# Revit family: FP-Revit19-en-OS60NMLG1-CombinationSteamOven-0-90003174A-AU-NZ-CN-IE-UK
name_source: partatom
category: Specialty Equipment
units: mm (PartAtom-declared; Revit-internal decimal feet)

## family parameters
Always vertical = Yes
Cut with Voids When Loaded = Yes
OmniClass Number = 23.40.40.14.17.11
OmniClass Title = Cookers, Ovens, Stoves
Part Type = Normal
Room Calculation Point = No
Round Connector Dimension = Use Diameter
Shared = No
Work Plane-Based = No

## types (1)
- OS60NMLG1
    Cavity - Depth = 550 mm
    Cavity - Height = 440 mm  [stored 1.44357 ft]
    Cavity - Width = 560 mm
    Chassis - Depth = 545 mm  [stored 1.78806 ft]
    Chassis - Height = 435 mm  [stored 1.42717 ft]
    Chassis - Width = 556 mm  [stored 1.82415 ft]
    Connector Description - Electrical = 220-240V, 50Hz ,15A
    Description = Combination Steam Oven, 60cm, 18 Function
    Manufacturer = Fisher & Paykel Appliances
    Material - Body = Fisher & Paykel - Grey
    Material - Dial = Fisher & Paykel - Aluminium, Dark, Matt
    Material - Glass = Fisher & Paykel - Glass, Grey
    Material - Handle = Fisher & Paykel - Aluminium, Dark
    Material - Structure = Fisher & Paykel - Black
    Material - Trim = Fisher & Paykel - Aluminium, Dark
    Model = OS60NMLG1
    Opening - Height = 460 mm  [stored 1.50919 ft]
    Product - Depth (Exc. Handles) = 565 mm  [stored 1.85367 ft]
    Product - Height = 458 mm
    Product - Width = 596 mm
    URL = www.fisherpaykel.com
    Visibility - Clearance Required = Yes

note: [stored X ft] marks values corroborated as IEEE doubles in the binary element streams (Revit-internal decimal feet)

## geometry (parser evidence)
native form markers: Sweep x12
no freeform markers — native parametric forms only
